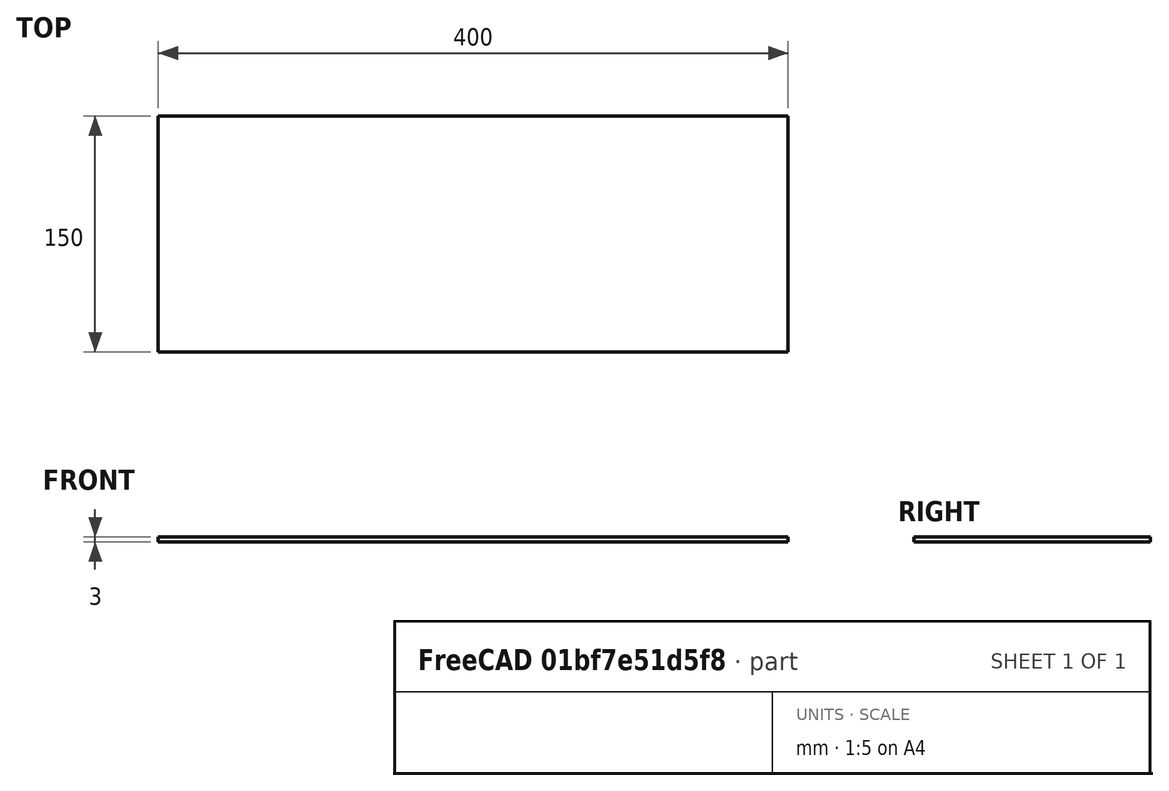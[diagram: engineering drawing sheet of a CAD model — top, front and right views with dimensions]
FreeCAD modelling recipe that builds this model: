
FCSTD DOCUMENT  (FreeCAD 0.18.4R)
Label: heater-base
License: All rights reserved
LicenseURL: http://en.wikipedia.org/wiki/All_rights_reserved
objects: Sketcher::SketchObject×1, PartDesign::Pad×1, PartDesign::Body×1
note: 4 computed .brp shape members not serialized (recipe doc carries the construction recipe); baked Part::Feature solids carry a one-line shape summary decoded from their .brp

FEATURE [Sketcher::SketchObject] Sketch
  MapMode = 5
  Support = -> [XY_Plane]
  sketch-geometry (4):
    g0: LineSegment StartX=-200 StartY=75 StartZ=0 EndX=200 EndY=75 EndZ=0
    g1: LineSegment StartX=200 StartY=75 StartZ=0 EndX=200 EndY=-75 EndZ=0
    g2: LineSegment StartX=200 StartY=-75 StartZ=0 EndX=-200 EndY=-75 EndZ=0
    g3: LineSegment StartX=-200 StartY=-75 StartZ=0 EndX=-200 EndY=75 EndZ=0
  constraints (12):
    c: Coincident(g0,g1)
    c: Coincident(g1,g2)
    c: Coincident(g2,g3)
    c: Coincident(g3,g0)
    c: Horizontal(g0)
    c: Horizontal(g2)
    c: Vertical(g1)
    c: Vertical(g3)
    c: DistanceX(g0,g0) = 400
    c: DistanceY(g-1,g0) = 75
    c: DistanceY(g3,g3) = 150
    c: DistanceX(g0,g-1) = 200
FEATURE [PartDesign::Pad] Pad
  Length = 3
  Length2 = 100
  Profile = -> Sketch
  Type = 0
FEATURE [PartDesign::Body] Body
  Group = -> [Sketch,Pad]
  Origin = -> Origin
  Tip = -> Pad
